# Revit family: PICO FP types Sans hôte
name_source: partatom
category: Dispositifs d'éclairage
units: mm (PartAtom-declared; Revit-internal decimal feet)

## family parameters
Basée sur le plan de construction = Oui
Conserver l'orientation des annotations = Non
Cote de connecteur circulaire = Utiliser le diamètre
Couper avec des vides une fois chargée = Non
Partagée = Non
Point de calcul de pièce = Non
Toujours verticalement = Oui
Type d'élément = Normal

## types (8) — shared parameters
Classe = 2
Code d'assemblage = D5010200
Fabricant = B.E.G.
Hauteur de montage max = 300 cm
Image du type = 360°.jpg
Marque = LUXOMAT
Mode de pose = Faux Plafond
URL = http://www.luxomat.com
zero-valued in all types: Elévation par défaut

## per-type parameters (varying)
| type | Alimentation | Charge Cos ɸ =0.5 | Charge Cos ɸ =1 | Charge LED | Commentaires du type | Consommation | IP | Modèle | Relais | Référence | Température ambiante | Type de Sortie |
| 01- PICO FP Générique | 110-240 V AC |  |  |  | MINI.DET.PRES.360°/Ø10M FAUX PLAFOND |  | 65 | PICO FP |  |  | -25°C à +50°C |  |
| 02- PICO N M 1C FP réf 93159 | 110-240 V AC | 1150 VA | 2300 W | 300 W | MINI.DET.PRES.MAITRE.1 CONTACT.360°/Ø10M FAUX PLAFOND | 0,35W | 65 | PICO N M 1C FP | 10 A | 93159 | -25°C à +50°C | TOR |
| 03- PICO S FP réf 92700 | 110-240 V AC | 0 | 0 | 0 | MINI.DET.PRES.ESCLAVE.360°/Ø10M FAUX PLAFOND | 0,25 W | 65 | PICO S FP | 0 | 92700 | -25°C à +50°C | Esclave |
| 05- PICO DALISYS FP réf 93909 | 10-22 V DC par Bus DALI | 0 | 0 | 0 | MINI.MULTI.CAPTEUR.PRES.DALISYS.360°/Ø10M FAUX PLAFOND | 2 mA | 20 | PICO DALISYS FP | 0 | 93909 | -25°C à +50°C | DALI Adressable |
| 07- PICO KNX DX FP réf 92719 | 24 V DC par Bus KNX | 0 | 0 | 0 | MINI.DET.PRES.KNX.VERSION DELUXE.360°/Ø10M FAUX PLAFOND | 12 mA | 20 | PICO KNX DX FP | 0 | 92719 | -25°C à +55°C | KNX - 1 sortie Eclairage TOR ou GRADATION / 3 sorties Présence / Capteur de température |
| 04- PICO DALILINK FP réf 93908 | 16 V DC par Bus DALI | 0 | 0 | 0 | MINI.MULTI.CAPTEUR.PRES.DALILINK.360°/Ø10M FAUX PLAFOND | 2 mA | 20 | PICO DALILINK FP | 0 | 93908 | -25°C à +50°C | DALILINK |
| 06- PICO BMS DALI 2 FP réf 93547 | 10-22 V DC par Bus DALI | 0 | 0 | 0 | MINI.MULTI.CAPTEUR.PRES.BMS.DALI 2.360°/Ø10M FAUX PLAFOND | 7 mA | 20 | PICO BMS DALI 2 FP | 0 | 93547 | -25°C à +50°C | DALI 2 Adressable |
| 08- PICO KNXs DX FP réf 93529 | 24 V DC par Bus KNX | 0 | 0 | 0 | MINI.DET.PRES.KNX Sécure.VERSION DELUXE.360°/Ø10M FAUX PLAFOND | 12 mA | 20 | PICO KNXs DX FP | 0 | 93529 | -25°C à +55°C | KNX Sécure - 1 sortie Eclairage TOR ou GRADATION / 3 sorties Présence / Capteur de température et bruit / HCL |
